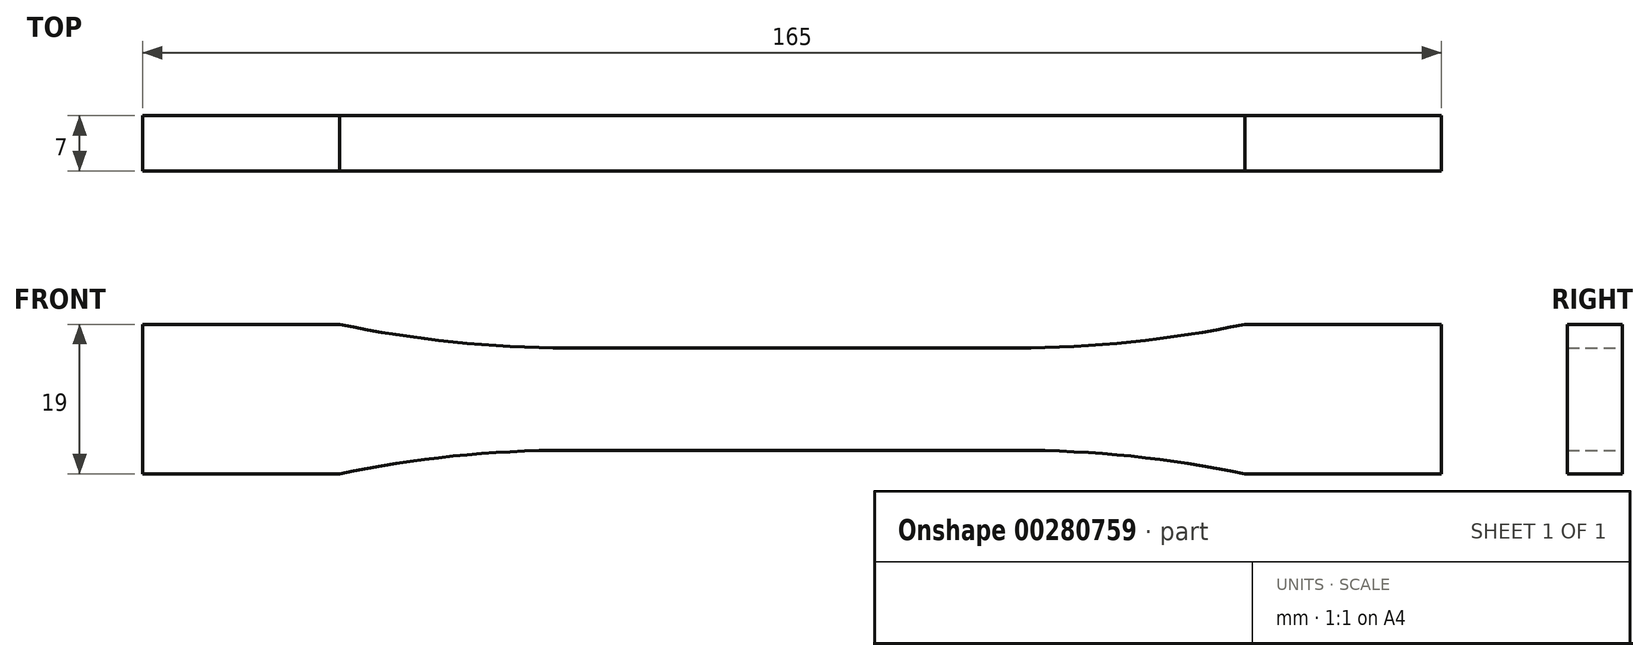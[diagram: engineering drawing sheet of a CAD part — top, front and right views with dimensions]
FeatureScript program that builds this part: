
annotation { "Feature Type Name" : "Feature", "Feature Type Description" : "" }
export const myFeature = defineFeature(function(context is Context, id is Id, definition is map)
    precondition{}
    {
        {
            var Q0;
            Q0=qCreatedBy(makeId("Front.planeOp"),FACE);
            var sketch = newSketch(context, id + "F0", { "sketchPlane" : qUnion([Q0])});
            skLineSegment(sketch, "E0", {"start": v(0, 6.5) * mm, "end": v(28.5, 6.5) * mm});
            skArc(sketch, "E1", {"start": v(28.5, 6.5) * mm, "mid": v(43.08, 7.25) * mm, "end": v(57.5, 9.5) * mm});
            skLineSegment(sketch, "E2", {"start": v(57.5, 9.5) * mm, "end": v(82.5, 9.5) * mm});
            skLineSegment(sketch, "E3.MirrorCS", {"start": v(0, -6.5) * mm, "end": v(28.5, -6.5) * mm});
            skLineSegment(sketch, "E4.MirrorCS", {"start": v(57.5, -9.5) * mm, "end": v(82.5, -9.5) * mm});
            skArc(sketch, "E5.MirrorCS", {"start": v(28.5, -6.5) * mm, "mid": v(43.08, -7.25) * mm, "end": v(57.5, -9.5) * mm});
            skArc(sketch, "E6.MirrorCS", {"start": v(-28.5, -6.5) * mm, "mid": v(-43.08, -7.25) * mm, "end": v(-57.5, -9.5) * mm});
            skLineSegment(sketch, "E7.MirrorCS", {"start": v(0, 6.5) * mm, "end": v(-28.5, 6.5) * mm});
            skArc(sketch, "E8.MirrorCS", {"start": v(-28.5, 6.5) * mm, "mid": v(-43.08, 7.25) * mm, "end": v(-57.5, 9.5) * mm});
            skLineSegment(sketch, "E9.MirrorCS", {"start": v(-57.5, -9.5) * mm, "end": v(-82.5, -9.5) * mm});
            skLineSegment(sketch, "E10.MirrorCS", {"start": v(-57.5, 9.5) * mm, "end": v(-82.5, 9.5) * mm});
            skLineSegment(sketch, "E11.MirrorCS", {"start": v(0, -6.5) * mm, "end": v(-28.5, -6.5) * mm});
            skLineSegment(sketch, "E12", {"start": v(-82.5, 9.5) * mm, "end": v(-82.5, -9.5) * mm});
            skLineSegment(sketch, "E13", {"start": v(82.5, 9.5) * mm, "end": v(82.5, -9.5) * mm});
            skSolve(sketch);
        }
        {
            var Q0;
            Q0=makeQuery(id+"F0.imprint","IMPRINT",FACE,{"disambiguationData":[TD([[makeQuery(id+"F0.imprint","IMPRINT",EDGE,{"derivedFrom":sQuery(id+"F0.wireOp",EDGE,"E0")}),-1.0]])]});
            extrude(context, id + "F1", {"entities" : qUnion([Q0]), "endBound" : BoundingType.SYMMETRIC, "depth" : 7 * mm});
        }
    });
